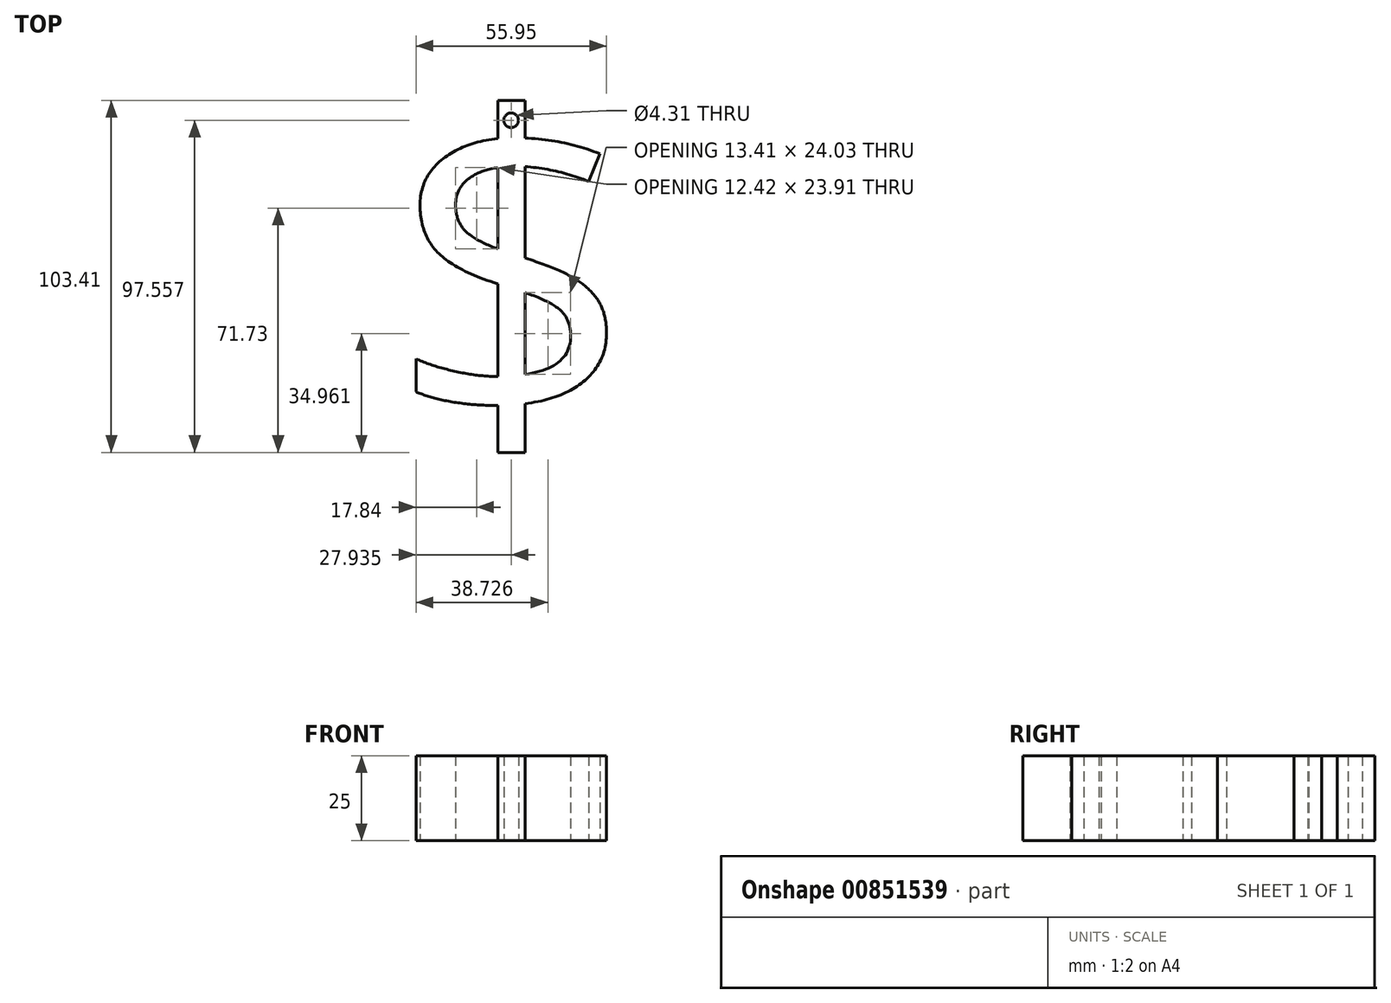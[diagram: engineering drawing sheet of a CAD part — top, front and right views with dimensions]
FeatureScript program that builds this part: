
annotation { "Feature Type Name" : "Feature", "Feature Type Description" : "" }
export const myFeature = defineFeature(function(context is Context, id is Id, definition is map)
    precondition{}
    {
        {
            var Q0;
            Q0=qCreatedBy(makeId("Top.planeOp"),FACE);
            var sketch = newSketch(context, id + "F0", { "sketchPlane" : qUnion([Q0])});
            skText(sketch, "E0", { "text": "$", "fontName": "OpenSans-Regular.ttf"});
            const initialGuessF0  = {"E0": [-0.04059, -0.05041, 1, 0, 0.09114]};
            skSetInitialGuess(sketch, initialGuessF0);
            skSolve(sketch);
        }
        {
            var Q0;
            Q0 = qSketchRegion(id + "F0", true);
            extrude(context, id + "F1", {"entities" : qUnion([Q0]), "depth" : 25 * mm, "offsetDistance" : 25 * mm});
        }
        {
            var Q0;
            Q0=qCreatedBy(makeId("Top.planeOp"),FACE);
            var sketch = newSketch(context, id + "F2", { "sketchPlane" : qUnion([Q0])});
            skCircle(sketch, "E1", {"center": v(-4.57, 39.79) * mm, "radius": 2.16 * mm});
            skSolve(sketch);
        }
        {
            var Q0;
            Q0 = qSketchRegion(id + "F2", true);
            extrude(context, id + "F3", {"entities" : qUnion([Q0]), "operationType" : NewBodyOperationType.REMOVE, "depth" : 25 * mm, "offsetDistance" : 25 * mm});
        }
    });
